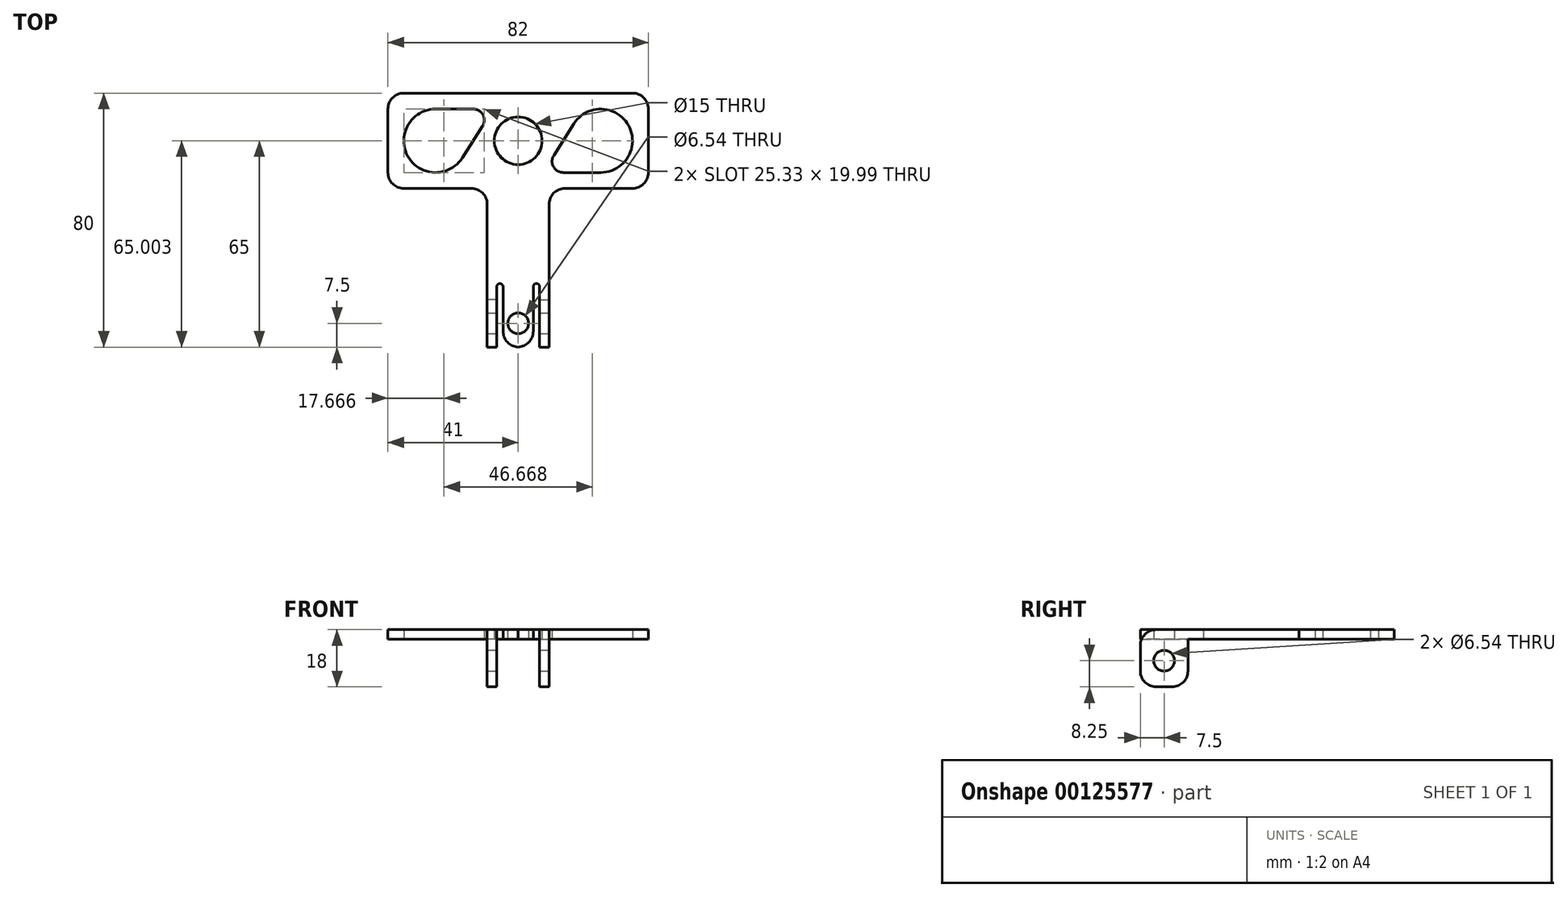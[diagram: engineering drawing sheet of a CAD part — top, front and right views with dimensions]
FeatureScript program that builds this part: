
annotation { "Feature Type Name" : "Feature", "Feature Type Description" : "" }
export const myFeature = defineFeature(function(context is Context, id is Id, definition is map)
    precondition{}
    {
        {
            assignVariable(context, id + "F0", {"name" : "R", "anyValue" : 7.5});
        }
        {
            var Q0;
            Q0=qCreatedBy(makeId("Top.planeOp"),FACE);
            var sketch = newSketch(context, id + "F1", { "sketchPlane" : qUnion([Q0])});
            skLineSegment(sketch, "E0.bottom", {"start": v(-41, 15) * mm, "end": v(41, 15) * mm});
            skLineSegment(sketch, "E0.top", {"start": v(-41, -15) * mm, "end": v(41, -15) * mm});
            skLineSegment(sketch, "E0.left", {"start": v(-41, 15) * mm, "end": v(-41, -15) * mm});
            skLineSegment(sketch, "E0.right", {"start": v(41, 15) * mm, "end": v(41, -15) * mm});
            skPoint(sketch, "E0.middle", {"position": v(0, 0) * mm});
            skArc(sketch, "E1", {"start": v(-26, 10) * mm, "mid": v(-34.76, -4.81) * mm, "end": v(-17.56, -5.36) * mm});
            skArc(sketch, "E2", {"start": v(-11.21, 4.62) * mm, "mid": v(-11.1, 8.19) * mm, "end": v(-14.17, 10) * mm});
            skCircle(sketch, "E3", {"center": v(0, 0) * mm, "radius": 7.5 * mm});
            skArc(sketch, "E4", {"start": v(26, -10) * mm, "mid": v(34.76, 4.81) * mm, "end": v(17.56, 5.36) * mm});
            skArc(sketch, "E5", {"start": v(11.21, -4.62) * mm, "mid": v(11.1, -8.19) * mm, "end": v(14.17, -10) * mm});
            skLineSegment(sketch, "E6", {"start": v(-26, 10) * mm, "end": v(-14.17, 10) * mm});
            skLineSegment(sketch, "E7", {"start": v(-11.21, 4.62) * mm, "end": v(-17.56, -5.36) * mm});
            skLineSegment(sketch, "E8", {"start": v(17.56, 5.36) * mm, "end": v(11.21, -4.62) * mm});
            skLineSegment(sketch, "E9", {"start": v(14.17, -10) * mm, "end": v(26, -10) * mm});
            skPoint(sketch, "E10", {"position": v(-36, 0) * mm});
            skPoint(sketch, "E11", {"position": v(36, 0) * mm});
            skPoint(sketch, "E11.positionSnap0", {"position": v(41, 0) * mm});
            skLineSegment(sketch, "E12", {"start": v(-9.75, -15) * mm, "end": v(-9.75, -65) * mm});
            skLineSegment(sketch, "E13", {"start": v(-9.75, -65) * mm, "end": v(-6.75, -65) * mm});
            skLineSegment(sketch, "E14", {"start": v(9.75, -65) * mm, "end": v(9.75, -15) * mm});
            skLineSegment(sketch, "E15", {"start": v(6.75, -65) * mm, "end": v(6.75, -45) * mm});
            skLineSegment(sketch, "E16", {"start": v(6.75, -45) * mm, "end": v(4.75, -45) * mm});
            skLineSegment(sketch, "E17", {"start": v(-6.75, -45) * mm, "end": v(-6.75, -65) * mm});
            skLineSegment(sketch, "E18.trimOffspring", {"start": v(6.75, -65) * mm, "end": v(9.75, -65) * mm});
            skLineSegment(sketch, "E19", {"start": v(4.75, -45) * mm, "end": v(4.75, -65) * mm});
            skLineSegment(sketch, "E20", {"start": v(4.75, -65) * mm, "end": v(-4.75, -65) * mm});
            skLineSegment(sketch, "E21", {"start": v(-4.75, -65) * mm, "end": v(-4.75, -45) * mm});
            skLineSegment(sketch, "E22.trimOffspring", {"start": v(-4.75, -45) * mm, "end": v(-6.75, -45) * mm});
            skCircle(sketch, "E23", {"center": v(0, -57.5) * mm, "radius": 3.27 * mm});
            skSolve(sketch);
        }
        {
            var Q0;
            Q0 = qSketchRegion(id + "F1", true);
            extrude(context, id + "F2", {"entities" : qUnion([Q0]), "depth" : 3 * mm});
        }
        {
            var Q0;
            Q0=makeQuery(id+"F2.opExtrude","CAP_FACE",FACE,{"disambiguationData":[OSD([sQuery(id+"F1.wireOp",EDGE,"E0.bottom"),sQuery(id+"F1.wireOp",EDGE,"E0.top"),sQuery(id+"F1.wireOp",EDGE,"E0.left"),sQuery(id+"F1.wireOp",EDGE,"E0.right"),sQuery(id+"F1.wireOp",EDGE,"E1"),sQuery(id+"F1.wireOp",EDGE,"E2"),sQuery(id+"F1.wireOp",EDGE,"E3"),sQuery(id+"F1.wireOp",EDGE,"E4"),sQuery(id+"F1.wireOp",EDGE,"E5"),sQuery(id+"F1.wireOp",EDGE,"E6"),sQuery(id+"F1.wireOp",EDGE,"E7"),sQuery(id+"F1.wireOp",EDGE,"E8"),sQuery(id+"F1.wireOp",EDGE,"E9"),sQuery(id+"F1.wireOp",EDGE,"E12"),sQuery(id+"F1.wireOp",EDGE,"E13"),sQuery(id+"F1.wireOp",EDGE,"E14"),sQuery(id+"F1.wireOp",EDGE,"E15"),sQuery(id+"F1.wireOp",EDGE,"E16"),sQuery(id+"F1.wireOp",EDGE,"E17"),sQuery(id+"F1.wireOp",EDGE,"E18.trimOffspring")])],"isStart":true});
            var sketch = newSketch(context, id + "F3", { "sketchPlane" : qUnion([Q0])});
            skLineSegment(sketch, "E24", {"start": v(9.75, 50) * mm, "end": v(9.75, 65) * mm});
            skLineSegment(sketch, "E25", {"start": v(9.75, 65) * mm, "end": v(6.75, 65) * mm});
            skLineSegment(sketch, "E26", {"start": v(6.75, 65) * mm, "end": v(6.75, 50) * mm});
            skLineSegment(sketch, "E27", {"start": v(6.75, 50) * mm, "end": v(9.75, 50) * mm});
            skLineSegment(sketch, "E28.MirrorCS", {"start": v(-6.75, 65) * mm, "end": v(-6.75, 50) * mm});
            skLineSegment(sketch, "E29.MirrorCS", {"start": v(-9.75, 65) * mm, "end": v(-6.75, 65) * mm});
            skLineSegment(sketch, "E30.MirrorCS", {"start": v(-9.75, 50) * mm, "end": v(-9.75, 65) * mm});
            skLineSegment(sketch, "E31.MirrorCS", {"start": v(-6.75, 50) * mm, "end": v(-9.75, 50) * mm});
            skSolve(sketch);
        }
        {
            var Q0;
            Q0=makeQuery(id+"F3.imprint","IMPRINT",FACE,{"disambiguationData":[TD([[makeQuery(id+"F3.imprint","IMPRINT",EDGE,{"derivedFrom":sQuery(id+"F3.wireOp",EDGE,"E24")}),-1.0]])]});
            var Q1;
            Q1=makeQuery(id+"F3.imprint","IMPRINT",FACE,{"disambiguationData":[TD([[makeQuery(id+"F3.imprint","IMPRINT",EDGE,{"derivedFrom":sQuery(id+"F3.wireOp",EDGE,"E28.MirrorCS")}),1.0]])]});
            extrude(context, id + "F4", {"entities" : qUnion([Q0, Q1]), "operationType" : NewBodyOperationType.ADD, "depth" : (2 * getVariable(context, 'R')) * mm});
        }
        {
            var Q0;
            Q0=makeQuery(id+"F4.boolean.opBoolean","MERGE",FACE,{"derivedFrom":[makeQuery(id+"F2.opExtrude","SWEPT_FACE",FACE,{"disambiguationData":[OSD([sQuery(id+"F1.wireOp",EDGE,"E14")])]}),makeQuery(id+"F4.opExtrude","SWEPT_FACE",FACE,{"disambiguationData":[OSD([sQuery(id+"F3.wireOp",EDGE,"E24")])]})]});
            var sketch = newSketch(context, id + "F5", { "sketchPlane" : qUnion([Q0])});
            skCircle(sketch, "E32", {"center": v(-57.5, -6.75) * mm, "radius": 3.27 * mm});
            skPoint(sketch, "E33", {"position": v(-65, 0) * mm});
            skPoint(sketch, "E34", {"position": v(-50, 0) * mm});
            skPoint(sketch, "E35", {"position": v(-57.5, 0) * mm});
            skSolve(sketch);
        }
        {
            var Q0;
            Q0 = qSketchRegion(id + "F5", true);
            extrude(context, id + "F6", {"entities" : qUnion([Q0]), "operationType" : NewBodyOperationType.REMOVE, "endBound" : BoundingType.THROUGH_ALL, "oppositeDirection" : true, "depth" : 25 * mm});
        }
        {
            var Q0;
            Q0=makeQuery(id+"F2.opExtrude","SWEPT_EDGE",EDGE,{"disambiguationData":[OSD([sQuery(id+"F1.wireOp",EDGE,"E0.bottom"),sQuery(id+"F1.wireOp",EDGE,"E0.left")])]});
            var Q1;
            Q1=makeQuery(id+"F2.opExtrude","SWEPT_EDGE",EDGE,{"disambiguationData":[OSD([sQuery(id+"F1.wireOp",EDGE,"E0.bottom"),sQuery(id+"F1.wireOp",EDGE,"E0.right")])]});
            var Q2;
            Q2=makeQuery(id+"F2.opExtrude","SWEPT_EDGE",EDGE,{"disambiguationData":[OSD([sQuery(id+"F1.wireOp",EDGE,"E0.top"),sQuery(id+"F1.wireOp",EDGE,"E0.right")])]});
            var Q3;
            Q3=makeQuery(id+"F2.opExtrude","SWEPT_EDGE",EDGE,{"disambiguationData":[OSD([sQuery(id+"F1.wireOp",EDGE,"E0.top"),sQuery(id+"F1.wireOp",EDGE,"E0.left")])]});
            var Q4;
            Q4=makeQuery(id+"F2.opExtrude","SWEPT_EDGE",EDGE,{"disambiguationData":[OSD([sQuery(id+"F1.wireOp",EDGE,"E0.top"),sQuery(id+"F1.wireOp",EDGE,"E12")])]});
            var Q5;
            Q5=makeQuery(id+"F2.opExtrude","SWEPT_EDGE",EDGE,{"disambiguationData":[OSD([sQuery(id+"F1.wireOp",EDGE,"E0.top"),sQuery(id+"F1.wireOp",EDGE,"E14")])]});
            var Q6;
            Q6=makeQuery(id+"F2.opExtrude","CAP_EDGE",EDGE,{"disambiguationData":[OSD([sQuery(id+"F1.wireOp",EDGE,"E13")])],"isStart":false});
            var Q7;
            Q7=makeQuery(id+"F4.opExtrude","CAP_EDGE",EDGE,{"disambiguationData":[OSD([sQuery(id+"F3.wireOp",EDGE,"E27")])],"isStart":true});
            var Q8;
            Q8=makeQuery(id+"F4.opExtrude","CAP_EDGE",EDGE,{"disambiguationData":[OSD([sQuery(id+"F3.wireOp",EDGE,"E31.MirrorCS")])],"isStart":true});
            var Q9;
            Q9=makeQuery(id+"F4.opExtrude","CAP_EDGE",EDGE,{"disambiguationData":[OSD([sQuery(id+"F3.wireOp",EDGE,"E31.MirrorCS")])],"isStart":false});
            var Q10;
            Q10=makeQuery(id+"F4.opExtrude","CAP_EDGE",EDGE,{"disambiguationData":[OSD([sQuery(id+"F3.wireOp",EDGE,"E27")])],"isStart":false});
            var Q11;
            Q11=makeQuery(id+"F4.opExtrude","CAP_EDGE",EDGE,{"disambiguationData":[OSD([sQuery(id+"F3.wireOp",EDGE,"E25")])],"isStart":false});
            var Q12;
            Q12=makeQuery(id+"F4.opExtrude","CAP_EDGE",EDGE,{"disambiguationData":[OSD([sQuery(id+"F3.wireOp",EDGE,"E29.MirrorCS")])],"isStart":false});
            var Q13;
            Q13=makeQuery(id+"F2.opExtrude","CAP_EDGE",EDGE,{"disambiguationData":[OSD([sQuery(id+"F1.wireOp",EDGE,"E18.trimOffspring")])],"isStart":false});
            var Q14;
            Q14=makeQuery(id+"F2.opExtrude","SWEPT_EDGE",EDGE,{"disambiguationData":[OSD([sQuery(id+"F1.wireOp",EDGE,"E19"),sQuery(id+"F1.wireOp",EDGE,"E20")])]});
            var Q15;
            Q15=makeQuery(id+"F2.opExtrude","SWEPT_EDGE",EDGE,{"disambiguationData":[OSD([sQuery(id+"F1.wireOp",EDGE,"E20"),sQuery(id+"F1.wireOp",EDGE,"E21")])]});
            fillet(context, id + "F7", {"entities" : qUnion([Q0, Q1, Q2, Q3, Q4, Q5, Q6, Q7, Q8, Q9, Q10, Q11, Q12, Q13, Q14, Q15]), "radius" : 5 * mm, "tangentPropagation" : true, "allowEdgeOverflow" : false});
        }
        {
            var Q0;
            Q0=makeQuery(id+"F2.opExtrude","SWEPT_EDGE",EDGE,{"disambiguationData":[OSD([sQuery(id+"F1.wireOp",EDGE,"E16"),sQuery(id+"F1.wireOp",EDGE,"E19")])]});
            var Q1;
            Q1=makeQuery(id+"F2.opExtrude","SWEPT_EDGE",EDGE,{"disambiguationData":[OSD([sQuery(id+"F1.wireOp",EDGE,"E15"),sQuery(id+"F1.wireOp",EDGE,"E16")])]});
            var Q2;
            Q2=makeQuery(id+"F2.opExtrude","SWEPT_EDGE",EDGE,{"disambiguationData":[OSD([sQuery(id+"F1.wireOp",EDGE,"E21"),sQuery(id+"F1.wireOp",EDGE,"E22.trimOffspring")])]});
            var Q3;
            Q3=makeQuery(id+"F2.opExtrude","SWEPT_EDGE",EDGE,{"disambiguationData":[OSD([sQuery(id+"F1.wireOp",EDGE,"E17"),sQuery(id+"F1.wireOp",EDGE,"E22.trimOffspring")])]});
            fillet(context, id + "F8", {"entities" : qUnion([Q0, Q1, Q2, Q3]), "radius" : 1 * mm, "tangentPropagation" : true, "allowEdgeOverflow" : false});
        }
    });
